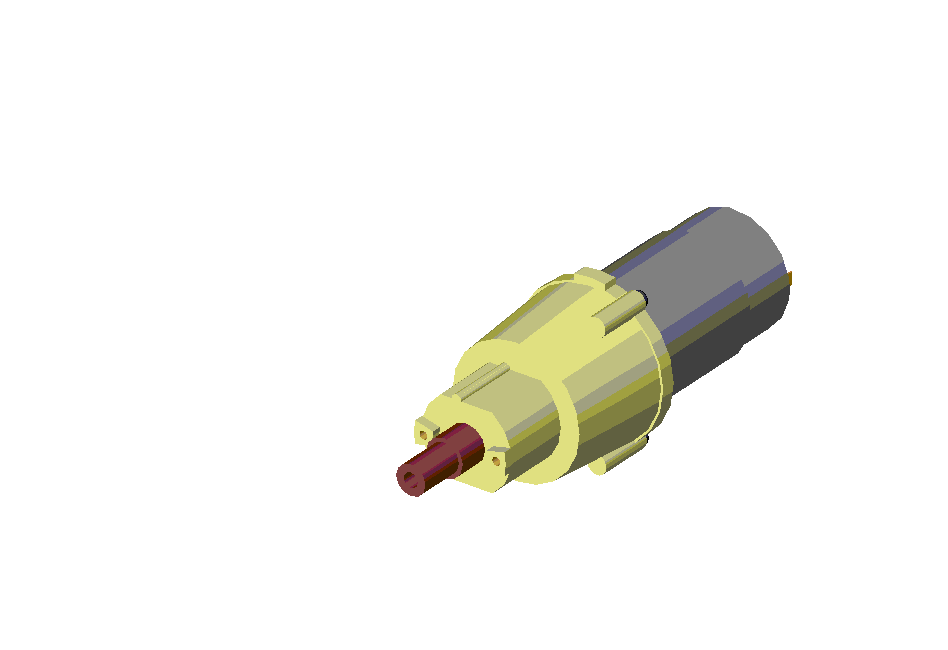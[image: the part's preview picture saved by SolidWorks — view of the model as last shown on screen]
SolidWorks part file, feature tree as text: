
SOLIDWORKS PART (.sldprt)
format: sldprt  version: not decoded by parser v0  size: 216,064 bytes
history: native  units: mm
features: sketch x20, extrude x16, cut_extrude x2, revolve x1, pattern_circular x1, plane x1, fillet x1 + 1 further entry (+4 scaffold rows collapsed)
feature tree (47):
  "Annotations"  RD1=36.592585mm
  revolve  "Boss-Revolve1"  [1 undecoded]
  sketch  "Sketch7"
  extrude  "Boss-Extrude3"  [1 undecoded]
  sketch  "Sketch5"  dims[D1=41.275mm D2=~48.525307mm D3=41.275mm]
  extrude  "Boss-Extrude2"  [1 undecoded]
  sketch  "Sketch3"  dims[c1.D5=15.748mm c1.D2=15.494mm c1.D3=29.2mm c2.D5=29.2mm c2.D1=3.2mm c2.D6=3.2mm c3.D1=29.718mm c3.D2=24.384mm c3.D3=24.384mm c3.D4=17.78mm c4.D1=~17.98066mm c4.D2=24.0mm c4.D4=12.0mm c4.D5=3.2mm c4.D7=6.4mm c5.D5=3.2mm]
  extrude  "Boss-Extrude1"  [1 undecoded]
  sketch  "Sketch2"  dims[D1=12.065mm]
  extrude  "Base-Extrude"  [1 undecoded]
  sketch  "Sketch1"  dims[c1.D1=9.525mm c2.D1=13.7922mm c3.D1=6.35mm c4.D1=21.336mm c5.D1=35.1mm c6.D1=360.0deg]
  extrude  "Boss-Extrude4"  [1 undecoded]
  sketch  "Sketch8"  dims[c1.D1=6.35mm c2.D1=17.526mm]
  pattern_circular  "CirPattern1"  Count=3  [1 undecoded]
  scaffold x4  (default folders/planes/origin — collapsed)
  sketch  "Sketch9"  dims[D1=37.8mm]
  extrude  "Boss-Extrude6"  Depth=40.005mm
  sketch  "Sketch13"
  sketch  "Sketch14"  dims[D1=35.6362mm]
  extrude  "Boss-Extrude7"  Depth=18.034mm
  sketch  "Sketch15"  dims[D1=15.494mm]
  extrude  "Boss-Extrude8"  Depth=2.9718mm
  sketch  "Sketch16"  dims[D1=3.0988mm]
  extrude  "Boss-Extrude9"  Depth=0.762mm
  sketch  "Sketch17"  dims[D1=1.905mm D2=3.81mm D3=0.5842mm D4=14.224mm D5=14.224mm D6=0.508mm D7=2.032mm D8=3.81mm]
  extrude  "Boss-Extrude10"  Depth=5.08mm
  sketch  "Sketch19"  dims[D1=17.78mm D2=~29.853247mm D3=3.556mm D4=7.112mm]
  extrude  "Boss-Extrude11"  Depth=2.9464mm
  sketch  "Sketch20"  dims[D3=2.54mm D4=2.54mm D1=11.811mm D2=11.811mm]
  cut_extrude  "Cut-Extrude1"  Depth=21.59mm
  sketch  "Sketch21"  dims[D1=12.065mm]
  extrude  "Boss-Extrude12"  Depth=9.652mm
  sketch  "Sketch22"
  extrude  "Boss-Extrude13"  Depth=24.13mm
  sketch  "Sketch23"  dims[D1=4.572mm]
  cut_extrude  "Cut-Extrude2"  Depth=21.59mm
  plane  "Plane1"
  sketch  "Sketch25"  dims[D1=47.44mm]
  extrude  "Boss-Extrude14"  Depth=4.56mm
  sketch  "Sketch26"  dims[c1.D1=51.26mm c1.D2=5.0mm c1.D3=10.0mm c1.D4=5.0mm c1.D5=10.0mm c2.D2=5.0mm c2.D3=10.0mm]
  extrude  "Boss-Extrude15"  [1 undecoded]
  sketch  "Sketch27"  dims[D1=5.4mm D2=5.4mm D3=5.4mm]
  extrude  "Boss-Extrude16"  Depth=2.2mm
  fillet  "Fillet1"  Radius=1mm
decode coverage: 31 of 41 modeling features carry decoded parameters; 1 rows unclassified (native names shown)
note: ~ marks probable driven/reference dimensions
note: 8 parameter values undecoded
summary: no parameter record found for 7 features
note: suppression state not decoded; provenance and decode notes live in map.json
